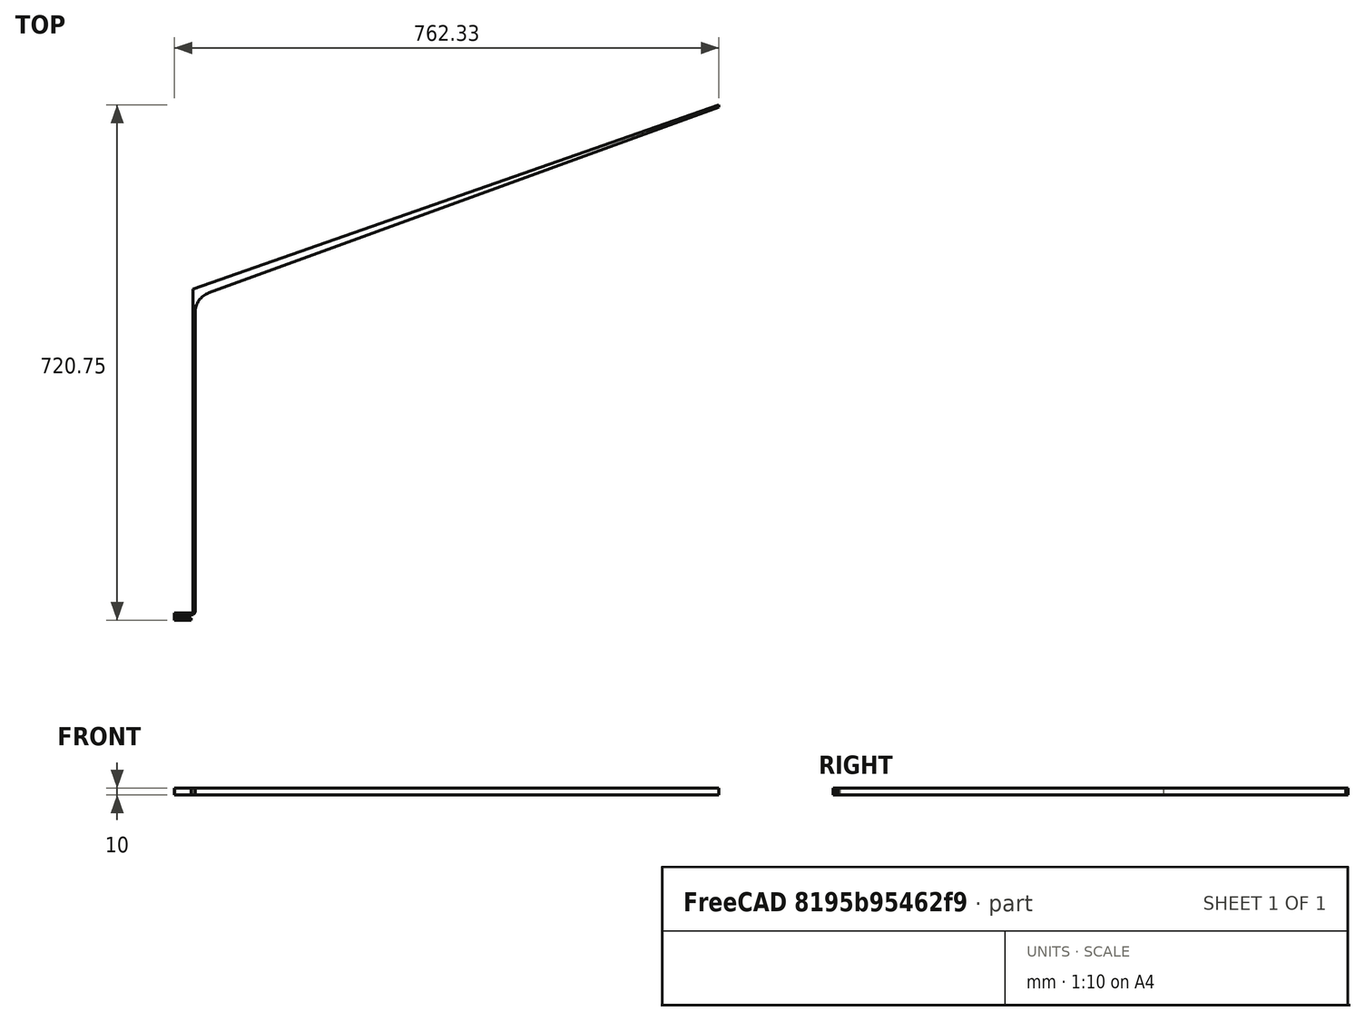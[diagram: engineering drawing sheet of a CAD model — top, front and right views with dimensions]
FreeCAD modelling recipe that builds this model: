
FCSTD DOCUMENT  (FreeCAD 0.22R38261 (Git))
Label: профиль лодки
License: All rights reserved
LicenseURL: https://en.wikipedia.org/wiki/All_rights_reserved
objects: Sketcher::SketchObject×1, PartDesign::Pad×1, PartDesign::Body×1
note: 5 computed .brp shape members not serialized (recipe doc carries the construction recipe); baked Part::Feature solids carry a one-line shape summary decoded from their .brp

FEATURE [Sketcher::SketchObject] Sketch
  AttachmentSupport = -> [XY_Plane]
  FullyConstrained = false
  MapMode = 5
  sketch-geometry (19):
    g0: LineSegment StartX=2.01223 StartY=0 StartZ=0 EndX=22.0122 EndY=0 EndZ=0
    g1: LineSegment StartX=0 StartY=-2.01223 StartZ=0 EndX=0 EndY=-2.01601 EndZ=0
    g2: LineSegment StartX=1.98399 StartY=-4 StartZ=0 EndX=21.984 EndY=-4 EndZ=0
    g3: LineSegment StartX=27.5725 StartY=5.56026 StartZ=0 EndX=27.5725 EndY=423.619 EndZ=0
    g4: ArcOfCircle CenterX=22.0122 CenterY=5.56026 CenterZ=0 NormalX=0 NormalY=0 NormalZ=1 AngleXU=0 Radius=5.56026 StartAngle=4.71239 EndAngle=6.28319
    g5: ArcOfCircle CenterX=1.98399 CenterY=-2.01601 CenterZ=0 NormalX=0 NormalY=0 NormalZ=1 AngleXU=0 Radius=1.98399 StartAngle=3.14159 EndAngle=4.71239
    g6: GeomPoint X=0 Y=-4 Z=0
    g7: ArcOfCircle CenterX=2.01223 CenterY=-2.01223 CenterZ=0 NormalX=0 NormalY=0 NormalZ=1 AngleXU=0 Radius=2.01223 StartAngle=1.5708 EndAngle=3.14159
    g8: GeomPoint X=0 Y=0 Z=0
    g9: LineSegment StartX=46.7017 StartY=450.938 StartZ=0 EndX=760.533 EndY=710.752 EndZ=0
    g10: ArcOfCircle CenterX=56.6452 CenterY=423.619 CenterZ=0 NormalX=0 NormalY=0 NormalZ=1 AngleXU=0 Radius=29.0727 StartAngle=1.91986 EndAngle=3.14159
    g11: GeomPoint X=27.5725 Y=443.976 Z=0
    g12: LineSegment StartX=21.984 StartY=-4 StartZ=0 EndX=21.984 EndY=-7 EndZ=0
    g13: LineSegment StartX=21.984 StartY=-7 StartZ=0 EndX=-1.80496 EndY=-7 EndZ=0
    g14: LineSegment StartX=-1.80496 StartY=-7 StartZ=0 EndX=-1.80496 EndY=3 EndZ=0
    g15: LineSegment StartX=-1.80496 StartY=3 StartZ=0 EndX=24.5725 EndY=3 EndZ=0
    g16: LineSegment StartX=24.5725 StartY=3 StartZ=0 EndX=24.5725 EndY=455.938 EndZ=0
    g17: LineSegment StartX=24.5725 StartY=455.938 StartZ=0 EndX=760.533 EndY=713.752 EndZ=0
    g18: LineSegment StartX=760.533 StartY=713.752 StartZ=0 EndX=760.533 EndY=710.752 EndZ=0
  constraints (43):
    c: Coincident(g8,g-1)
    c: PointOnObject(g6,g-2)
    c: Distance(g8,g6) = 4
    c: Horizontal(g2)
    c: Vertical(g3)
    c: Tangent(g0,g4) = -1.5708
    c: Tangent(g3,g4) = -1.5708
    c: PointOnObject(g6,g1)
    c: PointOnObject(g6,g2)
    c: Tangent(g1,g5) = -1.5708
    c: Tangent(g2,g5) = -1.5708
    c: PointOnObject(g8,g1)
    c: PointOnObject(g8,g0)
    c: Tangent(g1,g7) = -1.5708
    c: Tangent(g0,g7) = 1.5708
    c: Distance(g9,g11) = 780
    c: PointOnObject(g11,g3)
    c: PointOnObject(g11,g9)
    c: Tangent(g3,g10) = 1.5708
    c: Tangent(g9,g10) = 1.5708
    c: Angle(g3,g9) = 1.91986
    c: Horizontal(g0)
    c: Coincident(g12,g2)
    c: Vertical(g12)
    c: Coincident(g13,g12)
    c: Horizontal(g13)
    c: Coincident(g14,g13)
    c: Vertical(g14)
    c: Horizontal(g15)
    c: Coincident(g16,g15)
    c: Vertical(g16)
    c: Coincident(g17,g16)
    c: Coincident(g18,g17)
    c: Coincident(g18,g9)
    c: Distance(g12) = 3
    c: Coincident(g14,g15)
    c: DistanceY(g0,g14) = 3
    c: DistanceX(g15,g3) = 3
    c: Vertical(g18)
    c: DistanceY(g18,g18) = 3
    c: DistanceY(g9,g16) = 5
    c: DistanceX(g2,g2) = 20
    c: DistanceX(g0,g0) = 20
FEATURE [PartDesign::Pad] Pad
  Direction = (0,0,1)
  Length = 10
  Length2 = 10
  Profile = -> Sketch
  ReferenceAxis = -> Sketch [N_Axis]
  Suppressed = false
  Type = 0
FEATURE [PartDesign::Body] Body
  AllowCompound = false
  Group = -> [Sketch,Pad]
  Origin = -> Origin
  Tip = -> Pad
